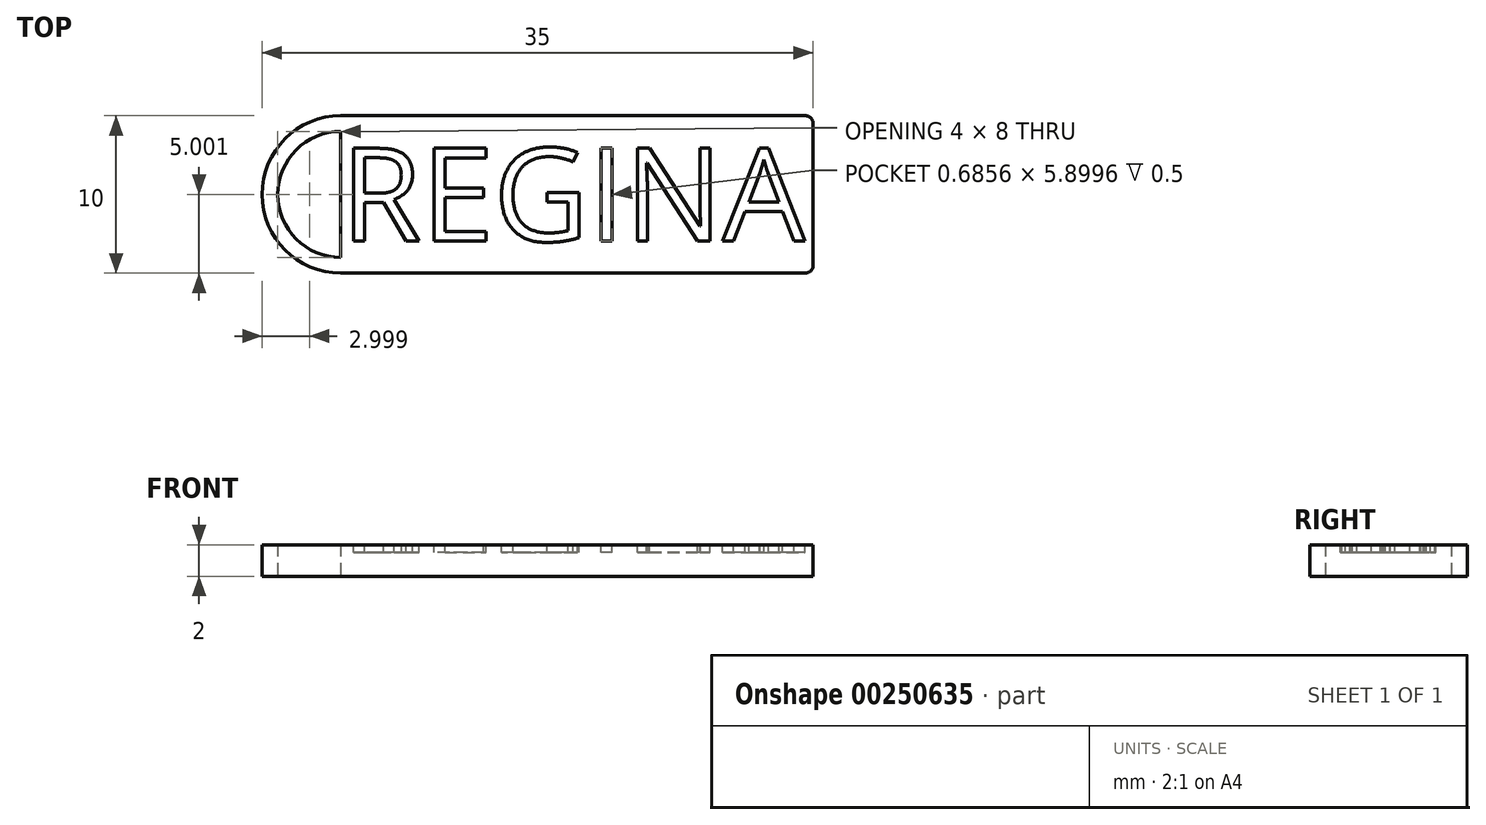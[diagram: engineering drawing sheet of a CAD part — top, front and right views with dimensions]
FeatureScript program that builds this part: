
annotation { "Feature Type Name" : "Feature", "Feature Type Description" : "" }
export const myFeature = defineFeature(function(context is Context, id is Id, definition is map)
    precondition{}
    {
        {
            var Q0;
            Q0=qCreatedBy(makeId("Top.planeOp"),FACE);
            var sketch = newSketch(context, id + "F0", { "sketchPlane" : qUnion([Q0])});
            skLineSegment(sketch, "E0.bottom", {"start": v(-5.27, 3.22) * mm, "end": v(24.73, 3.22) * mm});
            skLineSegment(sketch, "E0.top", {"start": v(-5.27, -6.78) * mm, "end": v(24.73, -6.78) * mm});
            skLineSegment(sketch, "E0.left", {"start": v(-5.27, 3.22) * mm, "end": v(-5.27, -6.78) * mm});
            skLineSegment(sketch, "E0.right", {"start": v(24.73, 3.22) * mm, "end": v(24.73, -6.78) * mm});
            skArc(sketch, "E1", {"start": v(-5.27, 3.22) * mm, "mid": v(-10.27, -1.78) * mm, "end": v(-5.27, -6.78) * mm});
            skArc(sketch, "E2", {"start": v(-5.27, 2.22) * mm, "mid": v(-9.27, -1.78) * mm, "end": v(-5.27, -5.78) * mm});
            skSolve(sketch);
        }
        {
            var Q0;
            Q0 = qSketchRegion(id + "F0", true);
            extrude(context, id + "F4", {"entities" : qUnion([Q0]), "depth" : 2 * mm});
        }
        {
            var Q0;
            Q0=makeQuery(id+"F4.opExtrude","CAP_FACE",FACE,{"disambiguationData":[OSD([sQuery(id+"F0.wireOp",EDGE,"E0.bottom"),sQuery(id+"F0.wireOp",EDGE,"E0.top"),sQuery(id+"F0.wireOp",EDGE,"E0.left"),sQuery(id+"F0.wireOp",EDGE,"E0.right")])],"isStart":false});
            var sketch = newSketch(context, id + "F1", { "sketchPlane" : qUnion([Q0])});
            skText(sketch, "E3", { "text": "REGINA", "fontName": "OpenSans-Regular.ttf"});
            skPoint(sketch, "E4", {"position": v(9.73, -1.78) * mm});
            skLineSegment(sketch, "E5", {"start": v(9.73, 3.22) * mm, "end": v(9.73, -6.78) * mm, "construction": true});
            const initialGuessF1  = {"E3": [-0.00527, -0.00475, 1, 0, 0.00595]};
            skSetInitialGuess(sketch, initialGuessF1);
            skSolve(sketch);
        }
        {
            var Q0;
            Q0 = qSketchRegion(id + "F1", true);
            extrude(context, id + "F2", {"entities" : qUnion([Q0]), "operationType" : NewBodyOperationType.REMOVE, "oppositeDirection" : true, "depth" : 0.5 * mm});
        }
        {
            var Q0;
            Q0=makeQuery(id+"F4.opExtrude","SWEPT_EDGE",EDGE,{"disambiguationData":[OSD([sQuery(id+"F0.wireOp",EDGE,"E0.top"),sQuery(id+"F0.wireOp",EDGE,"E0.right")])]});
            var Q1;
            Q1=makeQuery(id+"F4.opExtrude","SWEPT_EDGE",EDGE,{"disambiguationData":[OSD([sQuery(id+"F0.wireOp",EDGE,"E0.bottom"),sQuery(id+"F0.wireOp",EDGE,"E0.right")])]});
            fillet(context, id + "F3", {"entities" : qUnion([Q0, Q1]), "radius" : 0.5 * mm, "tangentPropagation" : true, "allowEdgeOverflow" : false});
        }
    });
